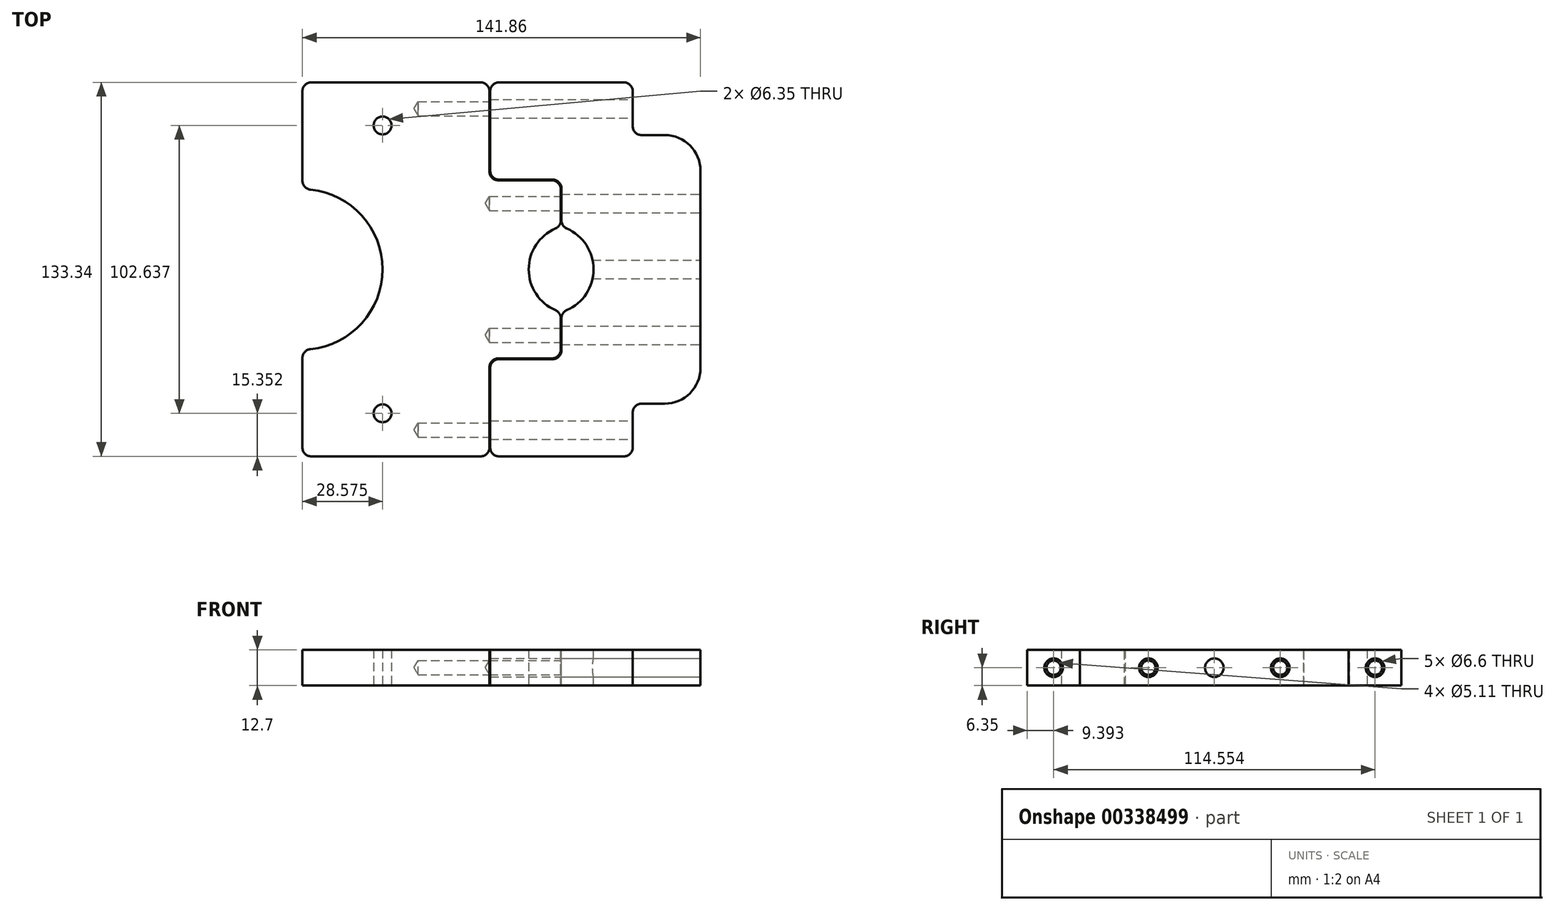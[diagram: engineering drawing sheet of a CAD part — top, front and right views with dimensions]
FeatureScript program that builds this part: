
annotation { "Feature Type Name" : "Feature", "Feature Type Description" : "" }
export const myFeature = defineFeature(function(context is Context, id is Id, definition is map)
    precondition{}
    {
        {
            var Q0;
            Q0=qCreatedBy(makeId("Top.planeOp"),FACE);
            var sketch = newSketch(context, id + "F0", { "sketchPlane" : qUnion([Q0])});
            skCircle(sketch, "E0", {"center": v(0, 0) * mm, "radius": 6.35 * mm});
            skSolve(sketch);
        }
        {
            var Q0;
            Q0=makeQuery(id+"F0.imprint","IMPRINT",FACE,{"disambiguationData":[TD([[makeQuery(id+"F0.imprint","IMPRINT",EDGE,{"derivedFrom":sQuery(id+"F0.wireOp",EDGE,"E0")}),1.0]])]});
            extrude(context, id + "F1", {"entities" : qUnion([Q0]), "oppositeDirection" : true, "depth" : 47.62 * mm});
        }
        {
            var Q0;
            Q0=makeQuery(id+"F1.opExtrude","CAP_FACE",FACE,{"disambiguationData":[OSD([sQuery(id+"F0.wireOp",EDGE,"E0")])],"isStart":true});
            var sketch = newSketch(context, id + "F2", { "sketchPlane" : qUnion([Q0])});
            skLineSegment(sketch, "E1", {"start": v(3.5, 5.3) * mm, "end": v(-3.5, 5.3) * mm});
            skSolve(sketch);
        }
        {
            var Q0;
            {var subQ0=sQuery(id+"F2.wireOp",EDGE,"E1");Q0=makeQuery(id+"F2.imprint","IMPRINT",FACE,{"disambiguationData":[TD([[makeQuery(id+"F2.imprint","IMPRINT",EDGE,{"derivedFrom":subQ0}),-1.0]])]});}
            extrude(context, id + "F3", {"entities" : qUnion([Q0]), "operationType" : NewBodyOperationType.REMOVE, "oppositeDirection" : true, "depth" : 31.75 * mm});
        }
        {
            var Q0;
            Q0=makeQuery(id+"F1.opExtrude","CAP_FACE",FACE,{"disambiguationData":[OSD([sQuery(id+"F0.wireOp",EDGE,"E0")])],"isStart":false});
            var sketch = newSketch(context, id + "F4", { "sketchPlane" : qUnion([Q0])});
            skCircle(sketch, "E2", {"center": v(0, 0) * mm, "radius": 18.73 * mm});
            skCircle(sketch, "E3", {"center": v(0, 0) * mm, "radius": 23.81 * mm});
            skSolve(sketch);
        }
        {
            var Q0;
            Q0=makeQuery(id+"F4.imprint","IMPRINT",FACE,{"disambiguationData":[TD([[makeQuery(id+"F4.imprint","IMPRINT",EDGE,{"derivedFrom":sQuery(id+"F4.wireOp",EDGE,"E2")}),-1.0]])]});
            extrude(context, id + "F5", {"entities" : qUnion([Q0]), "oppositeDirection" : true, "depth" : 20.32 * mm});
        }
        {
            var Q0;
            Q0=makeQuery(id+"F1.opExtrude","CAP_FACE",FACE,{"disambiguationData":[OSD([sQuery(id+"F0.wireOp",EDGE,"E0")])],"isStart":false});
            var sketch = newSketch(context, id + "F6", { "sketchPlane" : qUnion([Q0])});
            skCircle(sketch, "E4", {"center": v(0, 0) * mm, "radius": 54.61 * mm});
            skPoint(sketch, "E5", {"position": v(28.57, -51.32) * mm});
            skPoint(sketch, "E6", {"position": v(-28.57, -51.32) * mm});
            skPoint(sketch, "E7", {"position": v(-28.57, 51.32) * mm});
            skPoint(sketch, "E8", {"position": v(28.57, 51.32) * mm});
            skCircle(sketch, "E9", {"center": v(-28.57, -51.32) * mm, "radius": 2.22 * mm});
            skCircle(sketch, "E10", {"center": v(28.57, -51.32) * mm, "radius": 2.22 * mm});
            skCircle(sketch, "E11", {"center": v(28.57, 51.32) * mm, "radius": 2.22 * mm});
            skCircle(sketch, "E12", {"center": v(-28.57, 51.32) * mm, "radius": 2.22 * mm});
            skPoint(sketch, "E13", {"position": v(30.53, -45.28) * mm});
            skPoint(sketch, "E14", {"position": v(22.4, -49.8) * mm});
            skPoint(sketch, "E15", {"position": v(30.53, 45.28) * mm});
            skPoint(sketch, "E16", {"position": v(22.4, 49.8) * mm});
            skPoint(sketch, "E17", {"position": v(-22.4, 49.8) * mm});
            skPoint(sketch, "E18", {"position": v(-30.53, 45.28) * mm});
            skPoint(sketch, "E19", {"position": v(-30.53, -45.28) * mm});
            skPoint(sketch, "E20", {"position": v(-22.4, -49.8) * mm});
            skPoint(sketch, "E21", {"position": v(-31.84, -56.77) * mm});
            skPoint(sketch, "E22", {"position": v(32.57, -56.26) * mm});
            skPoint(sketch, "E23", {"position": v(32.06, 56.62) * mm});
            skPoint(sketch, "E24", {"position": v(-27.59, 57.6) * mm});
            skArc(sketch, "E25", {"start": v(22.4, -49.8) * mm, "mid": v(31.66, -56.87) * mm, "end": v(30.53, -45.28) * mm});
            skArc(sketch, "E26", {"start": v(-30.53, -45.28) * mm, "mid": v(-31.66, -56.87) * mm, "end": v(-22.4, -49.8) * mm});
            skArc(sketch, "E27", {"start": v(-22.4, 49.8) * mm, "mid": v(-31.66, 56.87) * mm, "end": v(-30.53, 45.28) * mm});
            skArc(sketch, "E28", {"start": v(30.53, 45.28) * mm, "mid": v(31.66, 56.87) * mm, "end": v(22.4, 49.8) * mm});
            skSolve(sketch);
        }
        {
            var Q0;
            Q0=makeQuery(id+"F6.imprint","IMPRINT",FACE,{"disambiguationData":[TD([[makeQuery(id+"F6.imprint","IMPRINT",EDGE,{"derivedFrom":sQuery(id+"F6.wireOp",EDGE,"E4")}),1.0]])]});
            var Q1;
            Q1=makeQuery(id+"F6.imprint","IMPRINT",FACE,{"disambiguationData":[TD([[makeQuery(id+"F6.imprint","IMPRINT",EDGE,{"derivedFrom":makeQuery(id+"F1.opExtrude","CAP_EDGE",EDGE,{"disambiguationData":[OSD([sQuery(id+"F0.wireOp",EDGE,"E0")])],"isStart":false})}),-1.0]])]});
            var Q2;
            Q2=makeQuery(id+"F6.imprint","IMPRINT",FACE,{"disambiguationData":[TD([[makeQuery(id+"F6.imprint","IMPRINT",EDGE,{"derivedFrom":sQuery(id+"F6.wireOp",EDGE,"E9")}),-1.0]])]});
            var Q3;
            Q3=makeQuery(id+"F6.imprint","IMPRINT",FACE,{"disambiguationData":[TD([[makeQuery(id+"F6.imprint","IMPRINT",EDGE,{"derivedFrom":sQuery(id+"F6.wireOp",EDGE,"E10")}),-1.0]])]});
            var Q4;
            Q4=makeQuery(id+"F6.imprint","IMPRINT",FACE,{"disambiguationData":[TD([[makeQuery(id+"F6.imprint","IMPRINT",EDGE,{"derivedFrom":sQuery(id+"F6.wireOp",EDGE,"E11")}),-1.0]])]});
            var Q5;
            Q5=makeQuery(id+"F6.imprint","IMPRINT",FACE,{"disambiguationData":[TD([[makeQuery(id+"F6.imprint","IMPRINT",EDGE,{"derivedFrom":sQuery(id+"F6.wireOp",EDGE,"E12")}),-1.0]])]});
            extrude(context, id + "F7", {"entities" : qUnion([Q0, Q1, Q2, Q3, Q4, Q5]), "depth" : 14.6 * mm});
        }
        {
            var Q0;
            Q0=makeQuery(id+"F7.opExtrude","CAP_FACE",FACE,{"disambiguationData":[OSD([sQuery(id+"F6.wireOp",EDGE,"E4")])],"isStart":false});
            var sketch = newSketch(context, id + "F8", { "sketchPlane" : qUnion([Q0])});
            skCircle(sketch, "E29", {"center": v(0, 0) * mm, "radius": 54.6 * mm});
            skSolve(sketch);
        }
        {
            var Q0;
            Q0=makeQuery(id+"F8.imprint","IMPRINT",FACE,{"disambiguationData":[TD([[makeQuery(id+"F8.imprint","IMPRINT",EDGE,{"derivedFrom":sQuery(id+"F8.wireOp",EDGE,"E29")}),1.0]])]});
            extrude(context, id + "F9", {"entities" : qUnion([Q0]), "operationType" : NewBodyOperationType.ADD, "depth" : 118.5 * mm});
        }
        {
            var Q0;
            Q0=makeQuery(id+"F9.opExtrude","CAP_FACE",FACE,{"disambiguationData":[OSD([sQuery(id+"F8.wireOp",EDGE,"E29")])],"isStart":false});
            var sketch = newSketch(context, id + "F10", { "sketchPlane" : qUnion([Q0])});
            skCircle(sketch, "E30", {"center": v(0, 0) * mm, "radius": 54.61 * mm});
            skSolve(sketch);
        }
        {
            var Q0;
            Q0=makeQuery(id+"F10.imprint","IMPRINT",FACE,{"disambiguationData":[TD([[makeQuery(id+"F10.imprint","IMPRINT",EDGE,{"derivedFrom":sQuery(id+"F10.wireOp",EDGE,"E30")}),1.0]])]});
            var Q1;
            Q1=makeQuery(id+"F10.imprint","IMPRINT",FACE,{"disambiguationData":[TD([[makeQuery(id+"F10.imprint","IMPRINT",EDGE,{"derivedFrom":makeQuery(id+"F9.opExtrude","CAP_EDGE",EDGE,{"disambiguationData":[OSD([sQuery(id+"F8.wireOp",EDGE,"E29")])],"isStart":false})}),1.0]])]});
            extrude(context, id + "F11", {"entities" : qUnion([Q0, Q1]), "operationType" : NewBodyOperationType.ADD, "depth" : 57.15 * mm});
        }
        {
            var Q0;
            Q0=makeQuery(id+"F7.opExtrude","CAP_FACE",FACE,{"disambiguationData":[OSD([sQuery(id+"F6.wireOp",EDGE,"E4")])],"isStart":true});
            var sketch = newSketch(context, id + "F12", { "sketchPlane" : qUnion([Q0])});
            skLineSegment(sketch, "E31", {"start": v(-44.45, 31.72) * mm, "end": v(44.45, 31.72) * mm});
            skPoint(sketch, "E32", {"position": v(0, 54.61) * mm});
            skArc(sketch, "E33", {"start": v(44.45, 31.72) * mm, "mid": v(0, 54.61) * mm, "end": v(-44.45, 31.72) * mm});
            skLineSegment(sketch, "E34", {"start": v(-44.45, 31.72) * mm, "end": v(-82.55, 31.72) * mm});
            skLineSegment(sketch, "E35", {"start": v(44.45, 31.72) * mm, "end": v(82.55, 31.72) * mm});
            skLineSegment(sketch, "E36", {"start": v(0, 54.61) * mm, "end": v(0, 67.31) * mm});
            skLineSegment(sketch, "E37", {"start": v(-82.55, 31.72) * mm, "end": v(-82.55, 44.42) * mm});
            skLineSegment(sketch, "E38", {"start": v(-82.55, 44.42) * mm, "end": v(-48.9, 44.42) * mm});
            skLineSegment(sketch, "E39", {"start": v(82.55, 31.72) * mm, "end": v(82.55, 44.42) * mm});
            skLineSegment(sketch, "E40", {"start": v(82.55, 44.42) * mm, "end": v(48.9, 44.42) * mm});
            skArc(sketch, "E41", {"start": v(48.9, 44.42) * mm, "mid": v(0, 67.31) * mm, "end": v(-48.9, 44.42) * mm});
            skSolve(sketch);
        }
        {
            var Q0;
            {var subQ0=sQuery(id+"F12.wireOp",EDGE,"E34");Q0=makeQuery(id+"F12.imprint","IMPRINT",FACE,{"disambiguationData":[TD([[makeQuery(id+"F12.imprint","IMPRINT",EDGE,{"derivedFrom":subQ0}),-1.0]])]});}
            var Q1;
            {var subQ0=sQuery(id+"F12.wireOp",EDGE,"E35");Q1=makeQuery(id+"F12.imprint","IMPRINT",FACE,{"disambiguationData":[TD([[makeQuery(id+"F12.imprint","IMPRINT",EDGE,{"derivedFrom":subQ0}),1.0]])]});}
            extrude(context, id + "F13", {"entities" : qUnion([Q0, Q1]), "oppositeDirection" : true, "depth" : 101.6 * mm});
        }
        {
            var Q0;
            Q0=makeQuery(id+"F7.opExtrude","CAP_FACE",FACE,{"disambiguationData":[OSD([sQuery(id+"F6.wireOp",EDGE,"E4")])],"isStart":true});
            var sketch = newSketch(context, id + "F14", { "sketchPlane" : qUnion([Q0])});
            skLineSegment(sketch, "E42", {"start": v(-44.45, -31.72) * mm, "end": v(44.45, -31.72) * mm});
            skPoint(sketch, "E43", {"position": v(0, -54.61) * mm});
            skArc(sketch, "E44", {"start": v(-44.45, -31.72) * mm, "mid": v(0, -54.61) * mm, "end": v(44.45, -31.72) * mm});
            skLineSegment(sketch, "E45", {"start": v(-44.45, -31.72) * mm, "end": v(-82.55, -31.72) * mm});
            skLineSegment(sketch, "E46", {"start": v(44.45, -31.72) * mm, "end": v(82.55, -31.72) * mm});
            skLineSegment(sketch, "E47", {"start": v(0, -54.61) * mm, "end": v(0, -67.31) * mm});
            skLineSegment(sketch, "E48", {"start": v(-82.55, -31.72) * mm, "end": v(-82.55, -44.42) * mm});
            skLineSegment(sketch, "E49", {"start": v(-82.55, -44.42) * mm, "end": v(-48.9, -44.42) * mm});
            skLineSegment(sketch, "E50", {"start": v(82.55, -31.72) * mm, "end": v(82.55, -44.42) * mm});
            skLineSegment(sketch, "E51", {"start": v(82.55, -44.42) * mm, "end": v(48.9, -44.42) * mm});
            skArc(sketch, "E52", {"start": v(-48.9, -44.42) * mm, "mid": v(0, -67.31) * mm, "end": v(48.9, -44.42) * mm});
            skSolve(sketch);
        }
        {
            var Q0;
            {var subQ0=sQuery(id+"F14.wireOp",EDGE,"E46");Q0=makeQuery(id+"F14.imprint","IMPRINT",FACE,{"disambiguationData":[TD([[makeQuery(id+"F14.imprint","IMPRINT",EDGE,{"derivedFrom":subQ0}),-1.0]])]});}
            var Q1;
            {var subQ0=sQuery(id+"F14.wireOp",EDGE,"E45");Q1=makeQuery(id+"F14.imprint","IMPRINT",FACE,{"disambiguationData":[TD([[makeQuery(id+"F14.imprint","IMPRINT",EDGE,{"derivedFrom":subQ0}),1.0]])]});}
            extrude(context, id + "F15", {"entities" : qUnion([Q0, Q1]), "oppositeDirection" : true, "depth" : 25.4 * mm});
        }
        {
            var Q0;
            {var subQ0=sQuery(id+"F14.wireOp",EDGE,"E49");var subQ2=sQuery(id+"F14.wireOp",EDGE,"E44");var subQ3=sQuery(id+"F14.wireOp",EDGE,"E45");var subQ4=sQuery(id+"F14.wireOp",EDGE,"E48");var subQ5=sQuery(id+"F14.wireOp",EDGE,"E52");Q0=makeQuery(id+"Fq8fBj3KPbGBi3Q_5.boolean.opBoolean","SPLIT",FACE,{"disambiguationData":[TD([makeQuery(id+"F15.opExtrude","SWEPT_FACE",FACE,{"disambiguationData":[OSD([subQ3])]})])],"derivedFrom":makeQuery(id+"F15.opExtrude","CAP_FACE",FACE,{"disambiguationData":[OSD([subQ2,subQ3,sQuery(id+"F14.wireOp",EDGE,"E46"),subQ4,subQ0,sQuery(id+"F14.wireOp",EDGE,"E50"),sQuery(id+"F14.wireOp",EDGE,"E51"),subQ5])],"isStart":false})});}
            var Q1;
            {var subQ0=sQuery(id+"F14.wireOp",EDGE,"E51");var subQ1=sQuery(id+"F14.wireOp",EDGE,"E50");var subQ2=sQuery(id+"F14.wireOp",EDGE,"E46");var subQ3=sQuery(id+"F14.wireOp",EDGE,"E44");var subQ4=sQuery(id+"F14.wireOp",EDGE,"E52");Q1=makeQuery(id+"Fq8fBj3KPbGBi3Q_5.boolean.opBoolean","SPLIT",FACE,{"disambiguationData":[TD([makeQuery(id+"F15.opExtrude","SWEPT_FACE",FACE,{"disambiguationData":[OSD([subQ2])]})])],"derivedFrom":makeQuery(id+"F15.opExtrude","CAP_FACE",FACE,{"disambiguationData":[OSD([subQ3,sQuery(id+"F14.wireOp",EDGE,"E45"),subQ2,sQuery(id+"F14.wireOp",EDGE,"E48"),sQuery(id+"F14.wireOp",EDGE,"E49"),subQ1,subQ0,subQ4])],"isStart":false})});}
            extrude(context, id + "F16", {"entities" : qUnion([Q0, Q1]), "operationType" : NewBodyOperationType.ADD, "depth" : 76.2 * mm});
        }
        {
            var Q0;
            Q0=makeQuery(id+"F16.opExtrude","CAP_FACE",FACE,{"disambiguationData":[OSD([sQuery(id+"F14.wireOp",EDGE,"E44"),sQuery(id+"F14.wireOp",EDGE,"E45"),sQuery(id+"F14.wireOp",EDGE,"E46"),sQuery(id+"F14.wireOp",EDGE,"E48"),sQuery(id+"F14.wireOp",EDGE,"E49"),sQuery(id+"F14.wireOp",EDGE,"E50"),sQuery(id+"F14.wireOp",EDGE,"E51"),sQuery(id+"F14.wireOp",EDGE,"E52")])],"isStart":false});
            var sketch = newSketch(context, id + "F17", { "sketchPlane" : qUnion([Q0])});
            skPoint(sketch, "E53", {"position": v(0, 67.31) * mm});
            skLineSegment(sketch, "E54", {"start": v(-38.1, 54.66) * mm, "end": v(-38.1, 87.68) * mm});
            skLineSegment(sketch, "E55", {"start": v(38.1, 54.66) * mm, "end": v(38.1, 87.68) * mm});
            skLineSegment(sketch, "E56", {"start": v(38.1, 87.68) * mm, "end": v(12.7, 87.68) * mm});
            skPoint(sketch, "E57", {"position": v(0, 76.2) * mm});
            skLineSegment(sketch, "E58", {"start": v(-38.1, 87.68) * mm, "end": v(-12.7, 87.68) * mm});
            skArc(sketch, "E59", {"start": v(-12.7, 87.68) * mm, "mid": v(0, 76.2) * mm, "end": v(12.7, 87.68) * mm});
            skSolve(sketch);
        }
        {
            var Q0;
            {var subQ0=sQuery(id+"F17.wireOp",EDGE,"E54");Q0=makeQuery(id+"F17.imprint","IMPRINT",FACE,{"disambiguationData":[TD([[makeQuery(id+"F17.imprint","IMPRINT",EDGE,{"derivedFrom":subQ0}),-1.0]])]});}
            extrude(context, id + "F18", {"entities" : qUnion([Q0]), "operationType" : NewBodyOperationType.ADD, "oppositeDirection" : true, "depth" : 76.2 * mm});
        }
        {
            var Q0;
            Q0=makeQuery(id+"F18.opExtrude","SWEPT_FACE",FACE,{"disambiguationData":[OSD([sQuery(id+"F17.wireOp",EDGE,"E58")])]});
            var sketch = newSketch(context, id + "F19", { "sketchPlane" : qUnion([Q0])});
            skCircle(sketch, "E60", {"center": v(-25.4, -85.72) * mm, "radius": 6.35 * mm});
            skCircle(sketch, "E61", {"center": v(-25.4, -111.12) * mm, "radius": 6.35 * mm});
            skCircle(sketch, "E62", {"center": v(-25.4, -136.53) * mm, "radius": 6.35 * mm});
            skCircle(sketch, "E63", {"center": v(25.17, -85.72) * mm, "radius": 6.35 * mm});
            skCircle(sketch, "E64", {"center": v(24.53, -111.12) * mm, "radius": 6.35 * mm});
            skCircle(sketch, "E65", {"center": v(25.35, -136.53) * mm, "radius": 6.35 * mm});
            skSolve(sketch);
        }
        {
            var Q0;
            Q0=sQuery(id+"F19.wireOp",VERTEX,"E60.center");
            var Q1;
            Q1=sQuery(id+"F19.wireOp",VERTEX,"E63.center");
            var Q2;
            Q2=sQuery(id+"F19.wireOp",VERTEX,"E61.center");
            var Q3;
            Q3=sQuery(id+"F19.wireOp",VERTEX,"E64.center");
            var Q4;
            Q4=sQuery(id+"F19.wireOp",VERTEX,"E62.center");
            var Q5;
            Q5=sQuery(id+"F19.wireOp",VERTEX,"E65.center");
            var Q6;
            Q6=makeQuery(id+"F15.opExtrude","SWEPT_BODY",BODY,{"disambiguationData":[OSD([sQuery(id+"F14.wireOp",EDGE,"E44"),sQuery(id+"F14.wireOp",EDGE,"E45"),sQuery(id+"F14.wireOp",EDGE,"E46"),sQuery(id+"F14.wireOp",EDGE,"E48"),sQuery(id+"F14.wireOp",EDGE,"E49"),sQuery(id+"F14.wireOp",EDGE,"E50"),sQuery(id+"F14.wireOp",EDGE,"E51"),sQuery(id+"F14.wireOp",EDGE,"E52")])]});
            hole(context, id + "F20", {"style" : HoleStyle.SIMPLE, "endStyle" : HoleEndStyle.BLIND, "holeDiameter" : 12.7 * mm, "holeDepth" : 12.7 * mm, "isTappedThrough" : true, "tappedDepth" : 12.7 * mm, "tapClearance" : 3, "startFromSketch" : true, "locations" : qUnion([Q0, Q1, Q2, Q3, Q4, Q5]), "scope" : qUnion([Q6])});
        }
        {
            var Q0;
            {var subQ0=sQuery(id+"F14.wireOp",EDGE,"E49");Q0=makeQuery(id+"F16.boolean.opBoolean","MERGE",FACE,{"derivedFrom":[makeQuery(id+"F15.opExtrude","SWEPT_FACE",FACE,{"disambiguationData":[OSD([subQ0])]}),makeQuery(id+"F16.opExtrude","SWEPT_FACE",FACE,{"disambiguationData":[OSD([subQ0])]})]});}
            var sketch = newSketch(context, id + "F21", { "sketchPlane" : qUnion([Q0])});
            skCircle(sketch, "E66", {"center": v(-69.85, -60.33) * mm, "radius": 6.35 * mm});
            skCircle(sketch, "E67", {"center": v(-69.85, -98.42) * mm, "radius": 6.35 * mm});
            skCircle(sketch, "E68", {"center": v(-69.85, -136.53) * mm, "radius": 6.35 * mm});
            skCircle(sketch, "E69", {"center": v(69.85, -60.33) * mm, "radius": 6.35 * mm});
            skCircle(sketch, "E70", {"center": v(69.85, -98.42) * mm, "radius": 6.35 * mm});
            skCircle(sketch, "E71", {"center": v(69.85, -136.53) * mm, "radius": 6.35 * mm});
            skSolve(sketch);
        }
        {
            var Q0;
            Q0=sQuery(id+"F21.wireOp",VERTEX,"E66.center");
            var Q1;
            Q1=sQuery(id+"F21.wireOp",VERTEX,"E67.center");
            var Q2;
            Q2=sQuery(id+"F21.wireOp",VERTEX,"E68.center");
            var Q3;
            Q3=sQuery(id+"F21.wireOp",VERTEX,"E69.center");
            var Q4;
            Q4=sQuery(id+"F21.wireOp",VERTEX,"E70.center");
            var Q5;
            Q5=sQuery(id+"F21.wireOp",VERTEX,"E71.center");
            var Q6;
            Q6=makeQuery(id+"F15.opExtrude","SWEPT_BODY",BODY,{"disambiguationData":[OSD([sQuery(id+"F14.wireOp",EDGE,"E44"),sQuery(id+"F14.wireOp",EDGE,"E45"),sQuery(id+"F14.wireOp",EDGE,"E46"),sQuery(id+"F14.wireOp",EDGE,"E48"),sQuery(id+"F14.wireOp",EDGE,"E49"),sQuery(id+"F14.wireOp",EDGE,"E50"),sQuery(id+"F14.wireOp",EDGE,"E51"),sQuery(id+"F14.wireOp",EDGE,"E52")])]});
            var Q7;
            Q7=makeQuery(id+"F13.opExtrude","SWEPT_BODY",BODY,{"disambiguationData":[OSD([sQuery(id+"F12.wireOp",EDGE,"E33"),sQuery(id+"F12.wireOp",EDGE,"E34"),sQuery(id+"F12.wireOp",EDGE,"E35"),sQuery(id+"F12.wireOp",EDGE,"E37"),sQuery(id+"F12.wireOp",EDGE,"E38"),sQuery(id+"F12.wireOp",EDGE,"E39"),sQuery(id+"F12.wireOp",EDGE,"E40"),sQuery(id+"F12.wireOp",EDGE,"E41")])]});
            hole(context, id + "F22", {"style" : HoleStyle.SIMPLE, "endStyle" : HoleEndStyle.THROUGH, "holeDiameter" : 12.7 * mm, "isTappedThrough" : true, "tappedDepth" : 12.7 * mm, "tapClearance" : 3, "startFromSketch" : true, "locations" : qUnion([Q0, Q1, Q2, Q3, Q4, Q5]), "scope" : qUnion([Q6, Q7])});
        }
        {
            var Q0;
            Q0=makeQuery(id+"F18.opExtrude","SWEPT_EDGE",EDGE,{"disambiguationData":[OSD([sQuery(id+"F14.wireOp",EDGE,"E52"),sQuery(id+"F17.wireOp",EDGE,"E54")])]});
            var Q1;
            Q1=makeQuery(id+"F18.opExtrude","CAP_EDGE",EDGE,{"disambiguationData":[OSD([sQuery(id+"F14.wireOp",EDGE,"E52")])],"isStart":false});
            var Q2;
            Q2=makeQuery(id+"F18.opExtrude","SWEPT_EDGE",EDGE,{"disambiguationData":[OSD([sQuery(id+"F14.wireOp",EDGE,"E52"),sQuery(id+"F17.wireOp",EDGE,"E55")])]});
            var Q3;
            {var subQ0=sQuery(id+"F14.wireOp",EDGE,"E52");var subQ1=sQuery(id+"F14.wireOp",EDGE,"E51");Q3=makeQuery(id+"F16.boolean.opBoolean","MERGE",EDGE,{"derivedFrom":[makeQuery(id+"F15.opExtrude","SWEPT_EDGE",EDGE,{"disambiguationData":[OSD([subQ1,subQ0])]}),makeQuery(id+"F16.opExtrude","SWEPT_EDGE",EDGE,{"disambiguationData":[OSD([subQ1,subQ0])]})]});}
            var Q4;
            {var subQ0=sQuery(id+"F14.wireOp",EDGE,"E52");var subQ1=sQuery(id+"F14.wireOp",EDGE,"E49");Q4=makeQuery(id+"F16.boolean.opBoolean","MERGE",EDGE,{"derivedFrom":[makeQuery(id+"F15.opExtrude","SWEPT_EDGE",EDGE,{"disambiguationData":[OSD([subQ1,subQ0])]}),makeQuery(id+"F16.opExtrude","SWEPT_EDGE",EDGE,{"disambiguationData":[OSD([subQ1,subQ0])]})]});}
            var Q5;
            Q5=makeQuery(id+"F13.opExtrude","SWEPT_EDGE",EDGE,{"disambiguationData":[OSD([sQuery(id+"F12.wireOp",EDGE,"E38"),sQuery(id+"F12.wireOp",EDGE,"E41")])]});
            var Q6;
            Q6=makeQuery(id+"F13.opExtrude","SWEPT_EDGE",EDGE,{"disambiguationData":[OSD([sQuery(id+"F12.wireOp",EDGE,"E40"),sQuery(id+"F12.wireOp",EDGE,"E41")])]});
            fillet(context, id + "F23", {"entities" : qUnion([Q0, Q1, Q2, Q3, Q4, Q5, Q6]), "radius" : 5.08 * mm, "tangentPropagation" : true, "allowEdgeOverflow" : false});
        }
        {
            var Q0;
            Q0=makeQuery(id+"F13.opExtrude","SWEPT_BODY",BODY,{"disambiguationData":[OSD([sQuery(id+"F12.wireOp",EDGE,"E33"),sQuery(id+"F12.wireOp",EDGE,"E34"),sQuery(id+"F12.wireOp",EDGE,"E35"),sQuery(id+"F12.wireOp",EDGE,"E37"),sQuery(id+"F12.wireOp",EDGE,"E38"),sQuery(id+"F12.wireOp",EDGE,"E39"),sQuery(id+"F12.wireOp",EDGE,"E40"),sQuery(id+"F12.wireOp",EDGE,"E41")])]});
            deleteBodies(context, id + "F24", {"entities" : qUnion([Q0])});
        }
        {
            var Q0;
            Q0=makeQuery(id+"F15.opExtrude","SWEPT_BODY",BODY,{"disambiguationData":[OSD([sQuery(id+"F14.wireOp",EDGE,"E44"),sQuery(id+"F14.wireOp",EDGE,"E45"),sQuery(id+"F14.wireOp",EDGE,"E46"),sQuery(id+"F14.wireOp",EDGE,"E48"),sQuery(id+"F14.wireOp",EDGE,"E49"),sQuery(id+"F14.wireOp",EDGE,"E50"),sQuery(id+"F14.wireOp",EDGE,"E51"),sQuery(id+"F14.wireOp",EDGE,"E52")])]});
            deleteBodies(context, id + "F25", {"entities" : qUnion([Q0])});
        }
        {
            var Q0;
            {var subQ0=sQuery(id+"F6.wireOp",EDGE,"E27");var subQ1=sQuery(id+"F6.wireOp",EDGE,"E4");Q0=makeQuery(id+"F7.opExtrude","SWEPT_EDGE",EDGE,{"disambiguationData":[OSD([subQ1,subQ0]),TDD([makeQuery(id+"F6.imprint","INTERSECT",VERTEX,{"disambiguationData":[OD(1.0)],"derivedFrom":[subQ1,subQ0]})])]});}
            var Q1;
            {var subQ0=sQuery(id+"F6.wireOp",EDGE,"E27");var subQ1=sQuery(id+"F6.wireOp",EDGE,"E4");Q1=makeQuery(id+"F7.opExtrude","SWEPT_EDGE",EDGE,{"disambiguationData":[OSD([subQ1,subQ0]),TDD([makeQuery(id+"F6.imprint","INTERSECT",VERTEX,{"disambiguationData":[OD(0.0)],"derivedFrom":[subQ1,subQ0]})])]});}
            var Q2;
            {var subQ0=sQuery(id+"F6.wireOp",EDGE,"E28");var subQ1=sQuery(id+"F6.wireOp",EDGE,"E4");Q2=makeQuery(id+"F7.opExtrude","SWEPT_EDGE",EDGE,{"disambiguationData":[OSD([subQ1,subQ0]),TDD([makeQuery(id+"F6.imprint","INTERSECT",VERTEX,{"disambiguationData":[OD(1.0)],"derivedFrom":[subQ1,subQ0]})])]});}
            var Q3;
            {var subQ0=sQuery(id+"F6.wireOp",EDGE,"E28");var subQ1=sQuery(id+"F6.wireOp",EDGE,"E4");Q3=makeQuery(id+"F7.opExtrude","SWEPT_EDGE",EDGE,{"disambiguationData":[OSD([subQ1,subQ0]),TDD([makeQuery(id+"F6.imprint","INTERSECT",VERTEX,{"disambiguationData":[OD(0.0)],"derivedFrom":[subQ1,subQ0]})])]});}
            var Q4;
            {var subQ0=sQuery(id+"F6.wireOp",EDGE,"E25");var subQ1=sQuery(id+"F6.wireOp",EDGE,"E4");Q4=makeQuery(id+"F7.opExtrude","SWEPT_EDGE",EDGE,{"disambiguationData":[OSD([subQ1,subQ0]),TDD([makeQuery(id+"F6.imprint","INTERSECT",VERTEX,{"disambiguationData":[OD(1.0)],"derivedFrom":[subQ1,subQ0]})])]});}
            var Q5;
            {var subQ0=sQuery(id+"F6.wireOp",EDGE,"E25");var subQ1=sQuery(id+"F6.wireOp",EDGE,"E4");Q5=makeQuery(id+"F7.opExtrude","SWEPT_EDGE",EDGE,{"disambiguationData":[OSD([subQ1,subQ0]),TDD([makeQuery(id+"F6.imprint","INTERSECT",VERTEX,{"disambiguationData":[OD(0.0)],"derivedFrom":[subQ1,subQ0]})])]});}
            var Q6;
            {var subQ0=sQuery(id+"F6.wireOp",EDGE,"E26");var subQ1=sQuery(id+"F6.wireOp",EDGE,"E4");Q6=makeQuery(id+"F7.opExtrude","SWEPT_EDGE",EDGE,{"disambiguationData":[OSD([subQ1,subQ0]),TDD([makeQuery(id+"F6.imprint","INTERSECT",VERTEX,{"disambiguationData":[OD(1.0)],"derivedFrom":[subQ1,subQ0]})])]});}
            var Q7;
            {var subQ0=sQuery(id+"F6.wireOp",EDGE,"E26");var subQ1=sQuery(id+"F6.wireOp",EDGE,"E4");Q7=makeQuery(id+"F7.opExtrude","SWEPT_EDGE",EDGE,{"disambiguationData":[OSD([subQ1,subQ0]),TDD([makeQuery(id+"F6.imprint","INTERSECT",VERTEX,{"disambiguationData":[OD(0.0)],"derivedFrom":[subQ1,subQ0]})])]});}
            fillet(context, id + "F26", {"entities" : qUnion([Q0, Q1, Q2, Q3, Q4, Q5, Q6, Q7]), "radius" : 6.35 * mm, "tangentPropagation" : true, "allowEdgeOverflow" : false});
        }
        {
            var Q0;
            Q0=qCreatedBy(makeId("Top.planeOp"),FACE);
            var sketch = newSketch(context, id + "F27", { "sketchPlane" : qUnion([Q0])});
            skPoint(sketch, "E72", {"position": v(0, -28.58) * mm});
            skPoint(sketch, "E73", {"position": v(0, -66.68) * mm});
            skPoint(sketch, "E74", {"position": v(0, 28.58) * mm});
            skPoint(sketch, "E75", {"position": v(0, 66.68) * mm});
            skPoint(sketch, "E76", {"position": v(28.58, 0) * mm});
            skArc(sketch, "E77", {"start": v(0, -28.58) * mm, "mid": v(28.58, 0) * mm, "end": v(0, 28.58) * mm});
            skLineSegment(sketch, "E78", {"start": v(0, -28.58) * mm, "end": v(0, -66.68) * mm});
            skLineSegment(sketch, "E79", {"start": v(0, 28.58) * mm, "end": v(0, 66.68) * mm});
            skPoint(sketch, "E80", {"position": v(66.68, 0) * mm});
            skLineSegment(sketch, "E81", {"start": v(0, -66.68) * mm, "end": v(66.68, -66.68) * mm});
            skPoint(sketch, "E82", {"position": v(66.68, -66.68) * mm});
            skLineSegment(sketch, "E83", {"start": v(0, 66.68) * mm, "end": v(66.68, 66.68) * mm});
            skPoint(sketch, "E84", {"position": v(66.68, 66.68) * mm});
            skPoint(sketch, "E85", {"position": v(66.68, -31.75) * mm});
            skPoint(sketch, "E86", {"position": v(66.68, 31.75) * mm});
            skLineSegment(sketch, "E87", {"start": v(66.68, -31.75) * mm, "end": v(92.08, -31.75) * mm});
            skLineSegment(sketch, "E88", {"start": v(92.08, 31.75) * mm, "end": v(66.68, 31.75) * mm});
            skLineSegment(sketch, "E89", {"start": v(66.68, -66.68) * mm, "end": v(66.68, -31.75) * mm});
            skLineSegment(sketch, "E90", {"start": v(66.68, 66.68) * mm, "end": v(66.68, 31.75) * mm});
            skPoint(sketch, "E91", {"position": v(92.08, 0) * mm});
            skPoint(sketch, "E92", {"position": v(92.08, -15.24) * mm});
            skPoint(sketch, "E93", {"position": v(92.08, 15.24) * mm});
            skPoint(sketch, "E94", {"position": v(80.65, 0) * mm});
            skArc(sketch, "E95", {"start": v(92.08, 15.24) * mm, "mid": v(80.65, 0) * mm, "end": v(92.08, -15.24) * mm});
            skLineSegment(sketch, "E96", {"start": v(92.08, -31.75) * mm, "end": v(92.08, -15.24) * mm});
            skLineSegment(sketch, "E97", {"start": v(92.08, 15.24) * mm, "end": v(92.08, 31.75) * mm});
            skPoint(sketch, "E98", {"position": v(28.57, -51.32) * mm});
            skPoint(sketch, "E99", {"position": v(28.57, 51.32) * mm});
            skCircle(sketch, "E100", {"center": v(28.57, 51.32) * mm, "radius": 3.18 * mm});
            skCircle(sketch, "E101", {"center": v(28.57, -51.32) * mm, "radius": 3.18 * mm});
            skSolve(sketch);
        }
        {
            var Q0;
            {var subQ16=sQuery(id+"F27.wireOp",EDGE,"E81");Q0=makeQuery(id+"F27.imprint","IMPRINT",FACE,{"disambiguationData":[TD([[makeQuery(id+"F27.imprint","IMPRINT",EDGE,{"derivedFrom":subQ16}),1.0]])]});}
            var Q1;
            {var subQ10=sQuery(id+"F27.wireOp",EDGE,"E77");Q1=makeQuery(id+"F27.imprint","IMPRINT",FACE,{"disambiguationData":[TD([[makeQuery(id+"F27.imprint","IMPRINT",EDGE,{"derivedFrom":subQ10}),-1.0]])]});}
            extrude(context, id + "F28", {"entities" : qUnion([Q0, Q1]), "operationType" : NewBodyOperationType.ADD, "depth" : 12.7 * mm});
        }
        {
            var Q0;
            Q0=makeQuery(id+"F1.opExtrude","SWEPT_BODY",BODY,{"disambiguationData":[OSD([sQuery(id+"F0.wireOp",EDGE,"E0")])]});
            deleteBodies(context, id + "F29", {"entities" : qUnion([Q0])});
        }
        {
            var Q0;
            Q0=makeQuery(id+"F5.opExtrude","SWEPT_BODY",BODY,{"disambiguationData":[OSD([sQuery(id+"F4.wireOp",EDGE,"E2"),sQuery(id+"F4.wireOp",EDGE,"E3")])]});
            deleteBodies(context, id + "F30", {"entities" : qUnion([Q0])});
        }
        {
            var Q0;
            Q0=makeQuery(id+"F7.opExtrude","SWEPT_BODY",BODY,{"disambiguationData":[OSD([sQuery(id+"F6.wireOp",EDGE,"E4"),sQuery(id+"F6.wireOp",EDGE,"E9"),sQuery(id+"F6.wireOp",EDGE,"E10"),sQuery(id+"F6.wireOp",EDGE,"E11"),sQuery(id+"F6.wireOp",EDGE,"E12"),sQuery(id+"F6.wireOp",EDGE,"E25"),sQuery(id+"F6.wireOp",EDGE,"E26"),sQuery(id+"F6.wireOp",EDGE,"E27"),sQuery(id+"F6.wireOp",EDGE,"E28")])]});
            deleteBodies(context, id + "F31", {"entities" : qUnion([Q0])});
        }
        {
            var Q0;
            Q0=makeQuery(id+"F28.opExtrude","CAP_FACE",FACE,{"disambiguationData":[OSD([sQuery(id+"F27.wireOp",EDGE,"E77"),sQuery(id+"F27.wireOp",EDGE,"E78"),sQuery(id+"F27.wireOp",EDGE,"E79"),sQuery(id+"F27.wireOp",EDGE,"E81"),sQuery(id+"F27.wireOp",EDGE,"E83"),sQuery(id+"F27.wireOp",EDGE,"E87"),sQuery(id+"F27.wireOp",EDGE,"E88"),sQuery(id+"F27.wireOp",EDGE,"E89"),sQuery(id+"F27.wireOp",EDGE,"E90"),sQuery(id+"F27.wireOp",EDGE,"E95"),sQuery(id+"F27.wireOp",EDGE,"E96"),sQuery(id+"F27.wireOp",EDGE,"E97"),sQuery(id+"F27.wireOp",EDGE,"E100"),sQuery(id+"F27.wireOp",EDGE,"E101")])],"isStart":false});
            var sketch = newSketch(context, id + "F32", { "sketchPlane" : qUnion([Q0])});
            skLineSegment(sketch, "E102", {"start": v(66.93, -66.68) * mm, "end": v(66.93, -32) * mm});
            skLineSegment(sketch, "E103", {"start": v(66.93, -32) * mm, "end": v(92.33, -32) * mm});
            skLineSegment(sketch, "E104", {"start": v(92.33, -32) * mm, "end": v(92.33, -15.24) * mm});
            skLineSegment(sketch, "E105", {"start": v(66.93, 66.68) * mm, "end": v(66.93, 32) * mm});
            skLineSegment(sketch, "E106", {"start": v(66.93, 32) * mm, "end": v(92.33, 32) * mm});
            skLineSegment(sketch, "E107", {"start": v(92.33, 32) * mm, "end": v(92.33, 15.24) * mm});
            skPoint(sketch, "E108", {"position": v(92.33, 0) * mm});
            skPoint(sketch, "E109", {"position": v(103.76, 0) * mm});
            skArc(sketch, "E110", {"start": v(92.33, -15.24) * mm, "mid": v(103.76, 0) * mm, "end": v(92.33, 15.24) * mm});
            skPoint(sketch, "E111", {"position": v(141.86, 0) * mm});
            skLineSegment(sketch, "E112", {"start": v(66.93, -66.68) * mm, "end": v(117.73, -66.68) * mm});
            skLineSegment(sketch, "E113", {"start": v(117.73, -66.68) * mm, "end": v(117.73, -47.88) * mm});
            skLineSegment(sketch, "E114", {"start": v(117.73, -47.88) * mm, "end": v(141.86, -47.88) * mm});
            skLineSegment(sketch, "E115", {"start": v(141.86, -47.88) * mm, "end": v(141.86, 0) * mm});
            skLineSegment(sketch, "E116", {"start": v(66.93, 66.68) * mm, "end": v(117.73, 66.68) * mm});
            skLineSegment(sketch, "E117", {"start": v(117.73, 66.68) * mm, "end": v(117.73, 47.88) * mm});
            skLineSegment(sketch, "E118", {"start": v(117.73, 47.88) * mm, "end": v(141.86, 47.88) * mm});
            skLineSegment(sketch, "E119", {"start": v(141.86, 47.88) * mm, "end": v(141.86, 0) * mm});
            skSolve(sketch);
        }
        {
            var Q0;
            Q0=makeQuery(id+"F32.imprint","IMPRINT",FACE,{"disambiguationData":[TD([[makeQuery(id+"F32.imprint","IMPRINT",EDGE,{"derivedFrom":sQuery(id+"F32.wireOp",EDGE,"E102")}),-1.0]])]});
            extrude(context, id + "F33", {"entities" : qUnion([Q0]), "oppositeDirection" : true, "depth" : 12.7 * mm});
        }
        {
            var Q0;
            Q0=makeQuery(id+"F28.opExtrude","SWEPT_EDGE",EDGE,{"disambiguationData":[OSD([sQuery(id+"F27.wireOp",EDGE,"E87"),sQuery(id+"F27.wireOp",EDGE,"E96")])]});
            var Q1;
            Q1=makeQuery(id+"F28.opExtrude","SWEPT_EDGE",EDGE,{"disambiguationData":[OSD([sQuery(id+"F27.wireOp",EDGE,"E87"),sQuery(id+"F27.wireOp",EDGE,"E89")])]});
            var Q2;
            Q2=makeQuery(id+"F28.opExtrude","SWEPT_EDGE",EDGE,{"disambiguationData":[OSD([sQuery(id+"F27.wireOp",EDGE,"E81"),sQuery(id+"F27.wireOp",EDGE,"E89")])]});
            var Q3;
            Q3=makeQuery(id+"F28.opExtrude","SWEPT_EDGE",EDGE,{"disambiguationData":[OSD([sQuery(id+"F27.wireOp",EDGE,"E95"),sQuery(id+"F27.wireOp",EDGE,"E96")])]});
            var Q4;
            Q4=makeQuery(id+"F28.opExtrude","SWEPT_EDGE",EDGE,{"disambiguationData":[OSD([sQuery(id+"F27.wireOp",EDGE,"E95"),sQuery(id+"F27.wireOp",EDGE,"E97")])]});
            var Q5;
            Q5=makeQuery(id+"F28.opExtrude","SWEPT_EDGE",EDGE,{"disambiguationData":[OSD([sQuery(id+"F27.wireOp",EDGE,"E88"),sQuery(id+"F27.wireOp",EDGE,"E97")])]});
            var Q6;
            Q6=makeQuery(id+"F28.opExtrude","SWEPT_EDGE",EDGE,{"disambiguationData":[OSD([sQuery(id+"F27.wireOp",EDGE,"E88"),sQuery(id+"F27.wireOp",EDGE,"E90")])]});
            var Q7;
            Q7=makeQuery(id+"F28.opExtrude","SWEPT_EDGE",EDGE,{"disambiguationData":[OSD([sQuery(id+"F27.wireOp",EDGE,"E83"),sQuery(id+"F27.wireOp",EDGE,"E90")])]});
            var Q8;
            Q8=makeQuery(id+"F28.opExtrude","SWEPT_EDGE",EDGE,{"disambiguationData":[OSD([sQuery(id+"F27.wireOp",EDGE,"E78"),sQuery(id+"F27.wireOp",EDGE,"E81")])]});
            var Q9;
            Q9=makeQuery(id+"F28.opExtrude","SWEPT_EDGE",EDGE,{"disambiguationData":[OSD([sQuery(id+"F27.wireOp",EDGE,"E77"),sQuery(id+"F27.wireOp",EDGE,"E78")])]});
            var Q10;
            Q10=makeQuery(id+"F28.opExtrude","SWEPT_EDGE",EDGE,{"disambiguationData":[OSD([sQuery(id+"F27.wireOp",EDGE,"E77"),sQuery(id+"F27.wireOp",EDGE,"E79")])]});
            var Q11;
            Q11=makeQuery(id+"F28.opExtrude","SWEPT_EDGE",EDGE,{"disambiguationData":[OSD([sQuery(id+"F27.wireOp",EDGE,"E79"),sQuery(id+"F27.wireOp",EDGE,"E83")])]});
            fillet(context, id + "F34", {"entities" : qUnion([Q0, Q1, Q2, Q3, Q4, Q5, Q6, Q7, Q8, Q9, Q10, Q11]), "radius" : 3.17 * mm, "allowEdgeOverflow" : false});
        }
        {
            var Q0;
            Q0=makeQuery(id+"F33.opExtrude","SWEPT_EDGE",EDGE,{"disambiguationData":[OSD([sQuery(id+"F32.wireOp",EDGE,"E105"),sQuery(id+"F32.wireOp",EDGE,"E106")])]});
            var Q1;
            Q1=makeQuery(id+"F33.opExtrude","SWEPT_EDGE",EDGE,{"disambiguationData":[OSD([sQuery(id+"F32.wireOp",EDGE,"E106"),sQuery(id+"F32.wireOp",EDGE,"E107")])]});
            var Q2;
            Q2=makeQuery(id+"F33.opExtrude","SWEPT_EDGE",EDGE,{"disambiguationData":[OSD([sQuery(id+"F32.wireOp",EDGE,"E107"),sQuery(id+"F32.wireOp",EDGE,"E110")])]});
            var Q3;
            Q3=makeQuery(id+"F33.opExtrude","SWEPT_EDGE",EDGE,{"disambiguationData":[OSD([sQuery(id+"F32.wireOp",EDGE,"E104"),sQuery(id+"F32.wireOp",EDGE,"E110")])]});
            var Q4;
            Q4=makeQuery(id+"F33.opExtrude","SWEPT_EDGE",EDGE,{"disambiguationData":[OSD([sQuery(id+"F32.wireOp",EDGE,"E103"),sQuery(id+"F32.wireOp",EDGE,"E104")])]});
            var Q5;
            Q5=makeQuery(id+"F33.opExtrude","SWEPT_EDGE",EDGE,{"disambiguationData":[OSD([sQuery(id+"F32.wireOp",EDGE,"E102"),sQuery(id+"F32.wireOp",EDGE,"E103")])]});
            var Q6;
            Q6=makeQuery(id+"F33.opExtrude","SWEPT_EDGE",EDGE,{"disambiguationData":[OSD([sQuery(id+"F32.wireOp",EDGE,"E105"),sQuery(id+"F32.wireOp",EDGE,"iKEHPpsS-4GlT-k21P-mxl7-VyM9v6ApYhEm")])]});
            var Q7;
            Q7=makeQuery(id+"F33.opExtrude","SWEPT_EDGE",EDGE,{"disambiguationData":[OSD([sQuery(id+"F32.wireOp",EDGE,"E102"),sQuery(id+"F32.wireOp",EDGE,"94xoSlKJ-d2HD-lKCy-Ixfv-d7kcOQUKirn8")])]});
            var Q8;
            Q8=makeQuery(id+"F33.opExtrude","SWEPT_EDGE",EDGE,{"disambiguationData":[OSD([sQuery(id+"F32.wireOp",EDGE,"ehCu32XG-8Vso-7YRo-K4Wa-oebUBLznHlxm"),sQuery(id+"F32.wireOp",EDGE,"94xoSlKJ-d2HD-lKCy-Ixfv-d7kcOQUKirn8")])]});
            var Q9;
            Q9=makeQuery(id+"F33.opExtrude","SWEPT_EDGE",EDGE,{"disambiguationData":[OSD([sQuery(id+"F32.wireOp",EDGE,"iwEpHMUa-1qKe-cbLA-zo8A-tS105tTPWSHH"),sQuery(id+"F32.wireOp",EDGE,"iKEHPpsS-4GlT-k21P-mxl7-VyM9v6ApYhEm")])]});
            var Q10;
            Q10=makeQuery(id+"F33.opExtrude","SWEPT_EDGE",EDGE,{"disambiguationData":[OSD([sQuery(id+"F32.wireOp",EDGE,"E112"),sQuery(id+"F32.wireOp",EDGE,"E113")])]});
            var Q11;
            Q11=makeQuery(id+"F33.opExtrude","SWEPT_EDGE",EDGE,{"disambiguationData":[OSD([sQuery(id+"F32.wireOp",EDGE,"E113"),sQuery(id+"F32.wireOp",EDGE,"E114")])]});
            var Q12;
            Q12=makeQuery(id+"F33.opExtrude","SWEPT_EDGE",EDGE,{"disambiguationData":[OSD([sQuery(id+"F32.wireOp",EDGE,"E116"),sQuery(id+"F32.wireOp",EDGE,"E117")])]});
            var Q13;
            Q13=makeQuery(id+"F33.opExtrude","SWEPT_EDGE",EDGE,{"disambiguationData":[OSD([sQuery(id+"F32.wireOp",EDGE,"E117"),sQuery(id+"F32.wireOp",EDGE,"E118")])]});
            fillet(context, id + "F35", {"entities" : qUnion([Q0, Q1, Q2, Q3, Q4, Q5, Q6, Q7, Q8, Q9, Q10, Q11, Q12, Q13]), "radius" : 3.17 * mm, "tangentPropagation" : true, "allowEdgeOverflow" : false});
        }
        {
            var Q0;
            Q0=makeQuery(id+"F33.opExtrude","SWEPT_EDGE",EDGE,{"disambiguationData":[OSD([sQuery(id+"F32.wireOp",EDGE,"E118"),sQuery(id+"F32.wireOp",EDGE,"E119")])]});
            var Q1;
            Q1=makeQuery(id+"F33.opExtrude","SWEPT_EDGE",EDGE,{"disambiguationData":[OSD([sQuery(id+"F32.wireOp",EDGE,"E114"),sQuery(id+"F32.wireOp",EDGE,"E115")])]});
            fillet(context, id + "F36", {"entities" : qUnion([Q0, Q1]), "radius" : 12.7 * mm, "tangentPropagation" : true, "allowEdgeOverflow" : false});
        }
        {
            var Q0;
            Q0=makeQuery(id+"F33.opExtrude","SWEPT_FACE",FACE,{"disambiguationData":[OSD([sQuery(id+"F32.wireOp",EDGE,"E113")])]});
            var sketch = newSketch(context, id + "F37", { "sketchPlane" : qUnion([Q0])});
            skPoint(sketch, "E120", {"position": v(-57.28, 6.35) * mm});
            skPoint(sketch, "E120.positionSnap0", {"position": v(-63.5, 6.35) * mm});
            skPoint(sketch, "E120.positionSnap1", {"position": v(-57.28, 12.7) * mm});
            skSolve(sketch);
        }
        {
            var Q0;
            Q0=sQuery(id+"F37.wireOp",VERTEX,"E120");
            var Q1;
            Q1=makeQuery(id+"F33.opExtrude","SWEPT_BODY",BODY,{"disambiguationData":[OSD([sQuery(id+"F32.wireOp",EDGE,"E102"),sQuery(id+"F32.wireOp",EDGE,"E103"),sQuery(id+"F32.wireOp",EDGE,"E104"),sQuery(id+"F32.wireOp",EDGE,"E105"),sQuery(id+"F32.wireOp",EDGE,"E106"),sQuery(id+"F32.wireOp",EDGE,"E107"),sQuery(id+"F32.wireOp",EDGE,"E110"),sQuery(id+"F32.wireOp",EDGE,"E112"),sQuery(id+"F32.wireOp",EDGE,"E113"),sQuery(id+"F32.wireOp",EDGE,"E114"),sQuery(id+"F32.wireOp",EDGE,"E115"),sQuery(id+"F32.wireOp",EDGE,"E116"),sQuery(id+"F32.wireOp",EDGE,"E117"),sQuery(id+"F32.wireOp",EDGE,"E118"),sQuery(id+"F32.wireOp",EDGE,"E119")])]});
            hole(context, id + "F38", {"style" : HoleStyle.SIMPLE, "endStyle" : HoleEndStyle.BLIND, "holeDiameter" : 6.6 * mm, "holeDepth" : 50.8 * mm, "isTappedThrough" : true, "tappedDepth" : 12.7 * mm, "tapClearance" : 3, "startFromSketch" : true, "locations" : qUnion([Q0]), "scope" : qUnion([Q1])});
        }
        {
            var Q0;
            Q0=makeQuery(id+"F33.opExtrude","SWEPT_FACE",FACE,{"disambiguationData":[OSD([sQuery(id+"F32.wireOp",EDGE,"E117")])]});
            var sketch = newSketch(context, id + "F39", { "sketchPlane" : qUnion([Q0])});
            skPoint(sketch, "E121", {"position": v(57.28, 6.35) * mm});
            skSolve(sketch);
        }
        {
            var Q0;
            Q0=sQuery(id+"F39.wireOp",VERTEX,"E121");
            var Q1;
            Q1=makeQuery(id+"F33.opExtrude","SWEPT_BODY",BODY,{"disambiguationData":[OSD([sQuery(id+"F32.wireOp",EDGE,"E102"),sQuery(id+"F32.wireOp",EDGE,"E103"),sQuery(id+"F32.wireOp",EDGE,"E104"),sQuery(id+"F32.wireOp",EDGE,"E105"),sQuery(id+"F32.wireOp",EDGE,"E106"),sQuery(id+"F32.wireOp",EDGE,"E107"),sQuery(id+"F32.wireOp",EDGE,"E110"),sQuery(id+"F32.wireOp",EDGE,"E112"),sQuery(id+"F32.wireOp",EDGE,"E113"),sQuery(id+"F32.wireOp",EDGE,"E114"),sQuery(id+"F32.wireOp",EDGE,"E115"),sQuery(id+"F32.wireOp",EDGE,"E116"),sQuery(id+"F32.wireOp",EDGE,"E117"),sQuery(id+"F32.wireOp",EDGE,"E118"),sQuery(id+"F32.wireOp",EDGE,"E119")])]});
            hole(context, id + "F40", {"style" : HoleStyle.SIMPLE, "endStyle" : HoleEndStyle.BLIND, "holeDiameter" : 6.6 * mm, "holeDepth" : 50.8 * mm, "isTappedThrough" : true, "tappedDepth" : 12.7 * mm, "tapClearance" : 3, "startFromSketch" : true, "locations" : qUnion([Q0]), "scope" : qUnion([Q1])});
        }
        {
            var Q0;
            Q0=makeQuery(id+"F33.opExtrude","SWEPT_FACE",FACE,{"disambiguationData":[OSD([sQuery(id+"F32.wireOp",EDGE,"E115"),sQuery(id+"F32.wireOp",EDGE,"E119")])]});
            var sketch = newSketch(context, id + "F41", { "sketchPlane" : qUnion([Q0])});
            skPoint(sketch, "E122", {"position": v(-23.5, 6.35) * mm});
            skPoint(sketch, "E123", {"position": v(23.5, 6.35) * mm});
            skPoint(sketch, "E124", {"position": v(0, 6.35) * mm});
            skPoint(sketch, "E124.positionSnap0", {"position": v(0, 12.7) * mm});
            skSolve(sketch);
        }
        {
            var Q0;
            Q0=sQuery(id+"F41.wireOp",VERTEX,"E122");
            var Q1;
            Q1=sQuery(id+"F41.wireOp",VERTEX,"E123");
            var Q2;
            Q2=sQuery(id+"F41.wireOp",VERTEX,"E124");
            var Q3;
            Q3=makeQuery(id+"F33.opExtrude","SWEPT_BODY",BODY,{"disambiguationData":[OSD([sQuery(id+"F32.wireOp",EDGE,"E102"),sQuery(id+"F32.wireOp",EDGE,"E103"),sQuery(id+"F32.wireOp",EDGE,"E104"),sQuery(id+"F32.wireOp",EDGE,"E105"),sQuery(id+"F32.wireOp",EDGE,"E106"),sQuery(id+"F32.wireOp",EDGE,"E107"),sQuery(id+"F32.wireOp",EDGE,"E110"),sQuery(id+"F32.wireOp",EDGE,"E112"),sQuery(id+"F32.wireOp",EDGE,"E113"),sQuery(id+"F32.wireOp",EDGE,"E114"),sQuery(id+"F32.wireOp",EDGE,"E115"),sQuery(id+"F32.wireOp",EDGE,"E116"),sQuery(id+"F32.wireOp",EDGE,"E117"),sQuery(id+"F32.wireOp",EDGE,"E118"),sQuery(id+"F32.wireOp",EDGE,"E119")])]});
            hole(context, id + "F42", {"style" : HoleStyle.SIMPLE, "endStyle" : HoleEndStyle.BLIND, "holeDiameter" : 6.6 * mm, "holeDepth" : 50.8 * mm, "isTappedThrough" : true, "tappedDepth" : 12.7 * mm, "tapClearance" : 3, "startFromSketch" : true, "locations" : qUnion([Q0, Q1, Q2]), "scope" : qUnion([Q3])});
        }
        {
            var Q0;
            Q0=makeQuery(id+"F28.opExtrude","SWEPT_FACE",FACE,{"disambiguationData":[OSD([sQuery(id+"F27.wireOp",EDGE,"E89")])]});
            var sketch = newSketch(context, id + "F43", { "sketchPlane" : qUnion([Q0])});
            skPoint(sketch, "E125", {"position": v(-57.28, 6.35) * mm});
            skPoint(sketch, "E125.positionSnap0", {"position": v(-63.5, 6.35) * mm});
            skSolve(sketch);
        }
        {
            var Q0;
            Q0=sQuery(id+"F43.wireOp",VERTEX,"E125");
            var Q1;
            Q1=makeQuery(id+"F28.opExtrude","SWEPT_BODY",BODY,{"disambiguationData":[OSD([sQuery(id+"F27.wireOp",EDGE,"E77"),sQuery(id+"F27.wireOp",EDGE,"E78"),sQuery(id+"F27.wireOp",EDGE,"E79"),sQuery(id+"F27.wireOp",EDGE,"E81"),sQuery(id+"F27.wireOp",EDGE,"E83"),sQuery(id+"F27.wireOp",EDGE,"E87"),sQuery(id+"F27.wireOp",EDGE,"E88"),sQuery(id+"F27.wireOp",EDGE,"E89"),sQuery(id+"F27.wireOp",EDGE,"E90"),sQuery(id+"F27.wireOp",EDGE,"E95"),sQuery(id+"F27.wireOp",EDGE,"E96"),sQuery(id+"F27.wireOp",EDGE,"E97"),sQuery(id+"F27.wireOp",EDGE,"E100"),sQuery(id+"F27.wireOp",EDGE,"E101")])]});
            hole(context, id + "F44", {"style" : HoleStyle.SIMPLE, "endStyle" : HoleEndStyle.BLIND, "standardTappedOrClearance" : lookupTablePath({ "standard" : "ANSI", "engagement" : "75%", "pitch" : "20 tpi", "size" : "1/4", "type" : "Tapped" }), "standardBlindInLast" : lookupTablePath({ "standard" : "ANSI", "engagement" : "75%", "pitch" : "20 tpi", "size" : "1/4", "type" : "Tapped" }), "holeDiameter" : 5.1 * mm, "showTappedDepth" : true, "holeDepth" : 25.4 * mm, "isTappedThrough" : true, "tappedDepth" : 21.59 * mm, "tapClearance" : 3, "startFromSketch" : true, "locations" : qUnion([Q0]), "scope" : qUnion([Q1]), "majorDiameter" : 6.35 * mm});
        }
        {
            var Q0;
            Q0=makeQuery(id+"F28.opExtrude","SWEPT_FACE",FACE,{"disambiguationData":[OSD([sQuery(id+"F27.wireOp",EDGE,"E90")])]});
            var sketch = newSketch(context, id + "F45", { "sketchPlane" : qUnion([Q0])});
            skPoint(sketch, "E126", {"position": v(57.28, 6.35) * mm});
            skPoint(sketch, "E126.positionSnap0", {"position": v(63.5, 6.35) * mm});
            skSolve(sketch);
        }
        {
            var Q0;
            Q0=sQuery(id+"F45.wireOp",VERTEX,"E126");
            var Q1;
            Q1=makeQuery(id+"F28.opExtrude","SWEPT_BODY",BODY,{"disambiguationData":[OSD([sQuery(id+"F27.wireOp",EDGE,"E77"),sQuery(id+"F27.wireOp",EDGE,"E78"),sQuery(id+"F27.wireOp",EDGE,"E79"),sQuery(id+"F27.wireOp",EDGE,"E81"),sQuery(id+"F27.wireOp",EDGE,"E83"),sQuery(id+"F27.wireOp",EDGE,"E87"),sQuery(id+"F27.wireOp",EDGE,"E88"),sQuery(id+"F27.wireOp",EDGE,"E89"),sQuery(id+"F27.wireOp",EDGE,"E90"),sQuery(id+"F27.wireOp",EDGE,"E95"),sQuery(id+"F27.wireOp",EDGE,"E96"),sQuery(id+"F27.wireOp",EDGE,"E97"),sQuery(id+"F27.wireOp",EDGE,"E100"),sQuery(id+"F27.wireOp",EDGE,"E101")])]});
            hole(context, id + "F46", {"style" : HoleStyle.SIMPLE, "endStyle" : HoleEndStyle.BLIND, "standardTappedOrClearance" : lookupTablePath({ "standard" : "ANSI", "engagement" : "75%", "pitch" : "20 tpi", "size" : "1/4", "type" : "Tapped" }), "standardBlindInLast" : lookupTablePath({ "standard" : "ANSI", "engagement" : "75%", "pitch" : "20 tpi", "size" : "1/4", "type" : "Tapped" }), "holeDiameter" : 5.1 * mm, "showTappedDepth" : true, "holeDepth" : 25.4 * mm, "isTappedThrough" : true, "tappedDepth" : 21.59 * mm, "tapClearance" : 3, "startFromSketch" : true, "locations" : qUnion([Q0]), "scope" : qUnion([Q1]), "majorDiameter" : 6.35 * mm});
        }
        {
            var Q0;
            Q0=makeQuery(id+"F28.opExtrude","SWEPT_FACE",FACE,{"disambiguationData":[OSD([sQuery(id+"F27.wireOp",EDGE,"E96")])]});
            var sketch = newSketch(context, id + "F47", { "sketchPlane" : qUnion([Q0])});
            skPoint(sketch, "E127", {"position": v(-23.5, 6.35) * mm});
            skPoint(sketch, "E127.positionSnap0", {"position": v(-28.57, 6.35) * mm});
            skPoint(sketch, "E128", {"position": v(23.5, 6.35) * mm});
            skSolve(sketch);
        }
        {
            var Q0;
            Q0=sQuery(id+"F47.wireOp",VERTEX,"E127");
            var Q1;
            Q1=sQuery(id+"F47.wireOp",VERTEX,"E128");
            var Q2;
            Q2=makeQuery(id+"F28.opExtrude","SWEPT_BODY",BODY,{"disambiguationData":[OSD([sQuery(id+"F27.wireOp",EDGE,"E77"),sQuery(id+"F27.wireOp",EDGE,"E78"),sQuery(id+"F27.wireOp",EDGE,"E79"),sQuery(id+"F27.wireOp",EDGE,"E81"),sQuery(id+"F27.wireOp",EDGE,"E83"),sQuery(id+"F27.wireOp",EDGE,"E87"),sQuery(id+"F27.wireOp",EDGE,"E88"),sQuery(id+"F27.wireOp",EDGE,"E89"),sQuery(id+"F27.wireOp",EDGE,"E90"),sQuery(id+"F27.wireOp",EDGE,"E95"),sQuery(id+"F27.wireOp",EDGE,"E96"),sQuery(id+"F27.wireOp",EDGE,"E97"),sQuery(id+"F27.wireOp",EDGE,"E100"),sQuery(id+"F27.wireOp",EDGE,"E101")])]});
            hole(context, id + "F48", {"style" : HoleStyle.SIMPLE, "endStyle" : HoleEndStyle.BLIND, "standardTappedOrClearance" : lookupTablePath({ "standard" : "ANSI", "engagement" : "75%", "pitch" : "20 tpi", "size" : "1/4", "type" : "Tapped" }), "standardBlindInLast" : lookupTablePath({ "standard" : "ANSI", "engagement" : "75%", "pitch" : "20 tpi", "size" : "1/4", "type" : "Tapped" }), "holeDiameter" : 5.1 * mm, "showTappedDepth" : true, "holeDepth" : 25.4 * mm, "isTappedThrough" : true, "tappedDepth" : 21.59 * mm, "tapClearance" : 3, "startFromSketch" : true, "locations" : qUnion([Q0, Q1]), "scope" : qUnion([Q2]), "majorDiameter" : 6.35 * mm});
        }
    });
